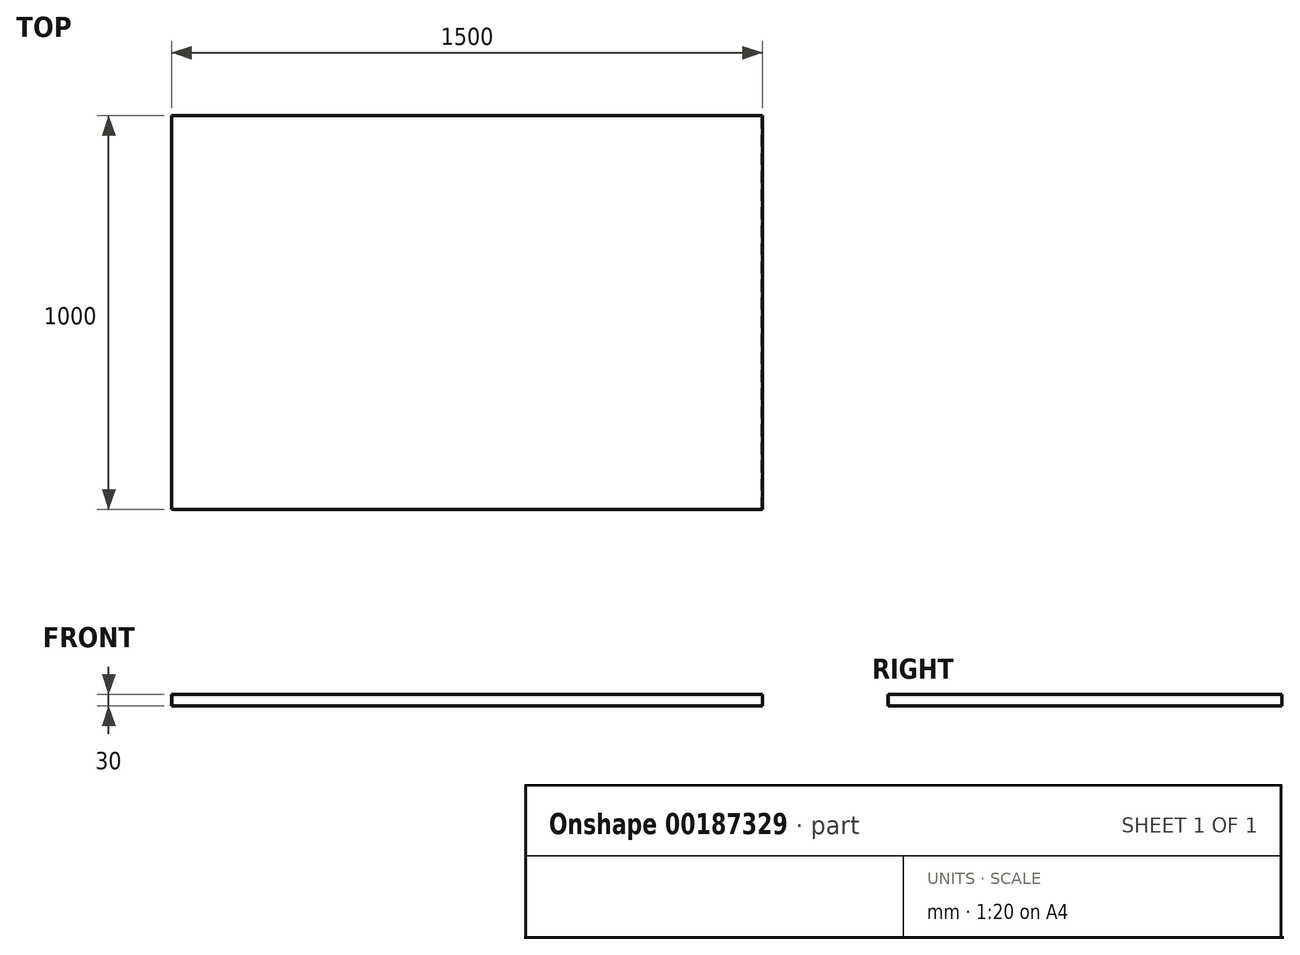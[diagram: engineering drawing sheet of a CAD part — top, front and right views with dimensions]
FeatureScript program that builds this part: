
annotation { "Feature Type Name" : "Feature", "Feature Type Description" : "" }
export const myFeature = defineFeature(function(context is Context, id is Id, definition is map)
    precondition{}
    {
        {
            var Q0;
            Q0=qCreatedBy(makeId("Top.planeOp"),FACE);
            var sketch = newSketch(context, id + "F0", { "sketchPlane" : qUnion([Q0])});
            skLineSegment(sketch, "E0.bottom", {"start": v(750, -500) * mm, "end": v(-750, -500) * mm});
            skLineSegment(sketch, "E0.top", {"start": v(750, 500) * mm, "end": v(-750, 500) * mm});
            skLineSegment(sketch, "E0.left", {"start": v(750, -500) * mm, "end": v(750, 500) * mm});
            skLineSegment(sketch, "E0.right", {"start": v(-750, -500) * mm, "end": v(-750, 500) * mm});
            skPoint(sketch, "E0.middle", {"position": v(0, 0) * mm});
            skSolve(sketch);
        }
        {
            var Q0;
            Q0=qSketchRegion(id+"F0",true);
            extrude(context, id + "F1", {"entities" : qUnion([Q0]), "depth" : 30 * mm});
        }
        {
            var Q0;
            Q0=makeQuery(id+"F1.opExtrude","CAP_FACE",FACE,{"disambiguationData":[OSD([sQuery(id+"F0.wireOp",EDGE,"E0.bottom"),sQuery(id+"F0.wireOp",EDGE,"E0.top"),sQuery(id+"F0.wireOp",EDGE,"E0.left"),sQuery(id+"F0.wireOp",EDGE,"E0.right")])],"isStart":true});
            shell(context, id + "F2", {"entities" : qUnion([Q0]), "thickness" : 1.6 * mm});
        }
    });
